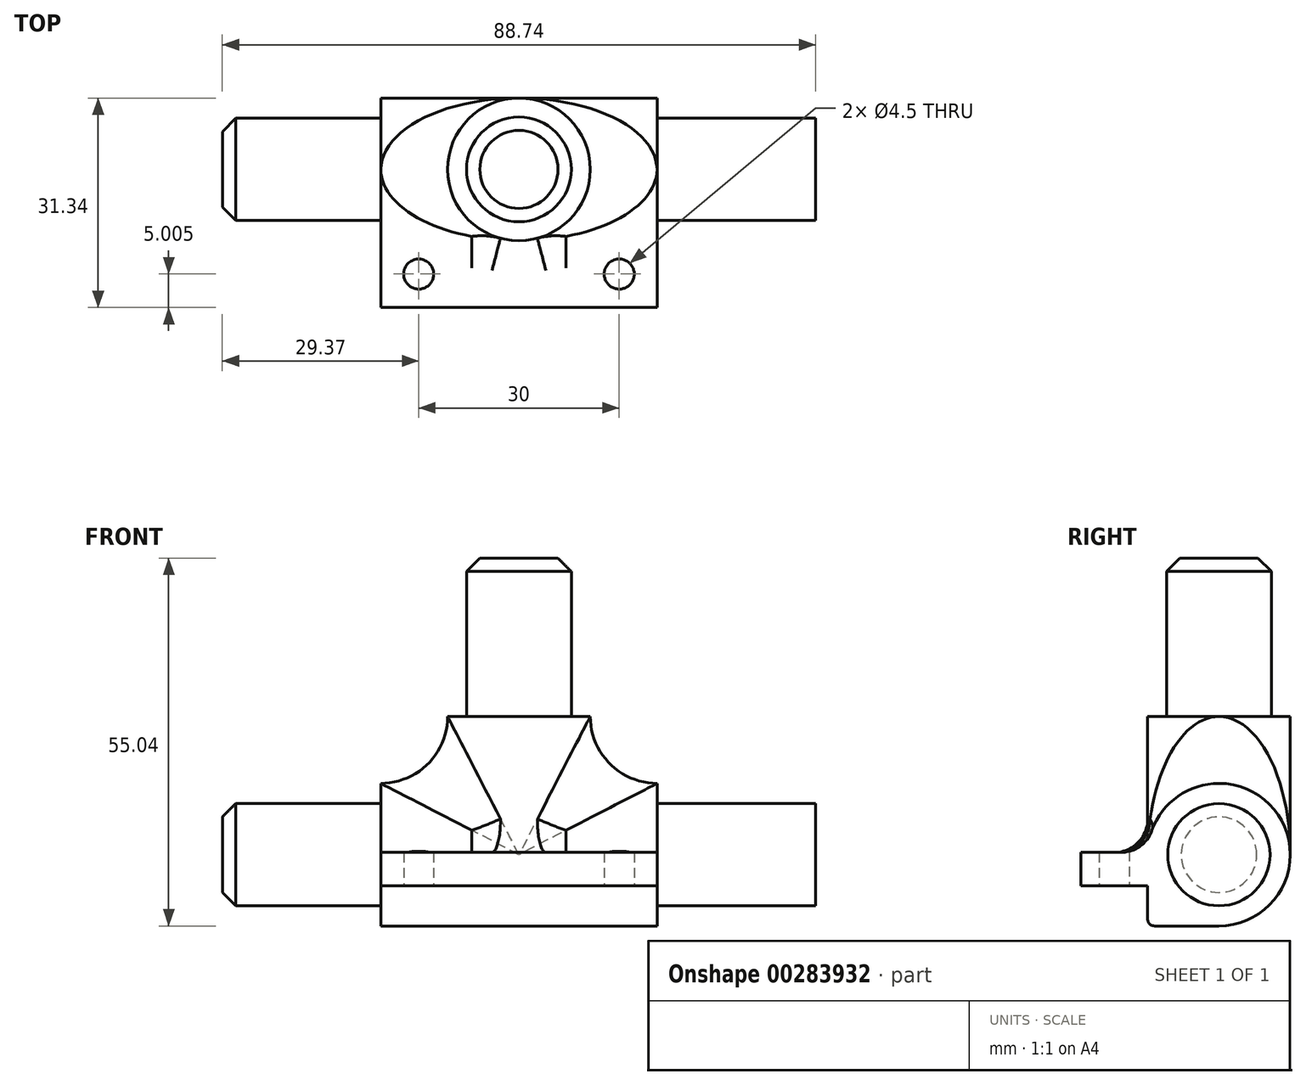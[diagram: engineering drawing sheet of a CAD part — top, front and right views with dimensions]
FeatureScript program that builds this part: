
annotation { "Feature Type Name" : "Feature", "Feature Type Description" : "" }
export const myFeature = defineFeature(function(context is Context, id is Id, definition is map)
    precondition{}
    {
        {
            var Q0;
            Q0=qCreatedBy(makeId("Right.planeOp"),FACE);
            var sketch = newSketch(context, id + "F0", { "sketchPlane" : qUnion([Q0])});
            skCircle(sketch, "E0", {"center": v(0, 0) * mm, "radius": 10.67 * mm});
            skSolve(sketch);
        }
        {
            var Q0;
            Q0 = qSketchRegion(id + "F0", true);
            extrude(context, id + "F1", {"entities" : qUnion([Q0]), "endBound" : BoundingType.SYMMETRIC, "depth" : 21.34 * mm + 20 * mm});
        }
        {
            var Q0;
            Q0=makeQuery(id+"F1.opExtrude","CAP_FACE",FACE,{"disambiguationData":[OSD([sQuery(id+"F0.wireOp",EDGE,"E0")])],"isStart":false});
            var sketch = newSketch(context, id + "F2", { "sketchPlane" : qUnion([Q0])});
            skCircle(sketch, "E1", {"center": v(0, 0) * mm, "radius": 7.9 * mm});
            skSolve(sketch);
        }
        {
            var Q0;
            Q0 = qSketchRegion(id + "F2", true);
            extrude(context, id + "F3", {"entities" : qUnion([Q0]), "operationType" : NewBodyOperationType.ADD, "depth" : 15.8 * mm * 1.5});
        }
        {
            var Q0;
            Q0=makeQuery(id+"F3.opExtrude","CAP_FACE",FACE,{"disambiguationData":[OSD([sQuery(id+"F2.wireOp",EDGE,"E1")])],"isStart":false});
            var sketch = newSketch(context, id + "F4", { "sketchPlane" : qUnion([Q0])});
            skCircle(sketch, "E2.0", {"center": v(0, 0) * mm, "radius": 7.9 * mm});
            skCircle(sketch, "E3", {"center": v(0, 0) * mm, "radius": 7.65 * mm});
            skSolve(sketch);
        }
        {
            var Q0;
            Q0 = qSketchRegion(id + "F4", true);
            var Q1;
            Q1=makeQuery(id+"F1.opExtrude","CAP_FACE",FACE,{"disambiguationData":[OSD([sQuery(id+"F0.wireOp",EDGE,"E0")])],"isStart":false});
            extrude(context, id + "F5", {"entities" : qUnion([Q0]), "operationType" : NewBodyOperationType.REMOVE, "endBound" : BoundingType.UP_TO_SURFACE, "oppositeDirection" : true, "endBoundEntityFace" : qUnion([Q1]), "depth" : 25 * mm});
        }
        {
            var Q0;
            Q0=makeQuery(id+"F1.opExtrude","CAP_FACE",FACE,{"disambiguationData":[OSD([sQuery(id+"F0.wireOp",EDGE,"E0")])],"isStart":true});
            var sketch = newSketch(context, id + "F6", { "sketchPlane" : qUnion([Q0])});
            skCircle(sketch, "E4", {"center": v(0, 0) * mm, "radius": 7.65 * mm});
            skSolve(sketch);
        }
        {
            var Q0;
            Q0 = qSketchRegion(id + "F6", true);
            extrude(context, id + "F7", {"entities" : qUnion([Q0]), "operationType" : NewBodyOperationType.ADD, "depth" : 15.8 * mm * 1.5});
        }
        {
            var Q0;
            Q0=qCreatedBy(makeId("Top.planeOp"),FACE);
            var sketch = newSketch(context, id + "F8", { "sketchPlane" : qUnion([Q0])});
            skCircle(sketch, "E5", {"center": v(0, 0) * mm, "radius": 10.67 * mm});
            skSolve(sketch);
        }
        {
            var Q0;
            Q0 = qSketchRegion(id + "F8", true);
            extrude(context, id + "F9", {"entities" : qUnion([Q0]), "operationType" : NewBodyOperationType.ADD, "depth" : 21.34 * mm / 2 + 10 * mm});
        }
        {
            var Q0;
            Q0=makeQuery(id+"F9.opExtrude","CAP_FACE",FACE,{"disambiguationData":[OSD([sQuery(id+"F8.wireOp",EDGE,"E5")])],"isStart":false});
            var sketch = newSketch(context, id + "F10", { "sketchPlane" : qUnion([Q0])});
            skCircle(sketch, "E6", {"center": v(0, 0) * mm, "radius": 7.84 * mm});
            skSolve(sketch);
        }
        {
            var Q0;
            Q0 = qSketchRegion(id + "F10", true);
            extrude(context, id + "F11", {"entities" : qUnion([Q0]), "operationType" : NewBodyOperationType.ADD, "depth" : 15.8 * mm * 1.5});
        }
        {
            var Q0;
            Q0=makeQuery(id+"F11.opExtrude","CAP_EDGE",EDGE,{"disambiguationData":[OSD([sQuery(id+"F10.wireOp",EDGE,"E6")])],"isStart":false});
            var Q1;
            Q1=makeQuery(id+"F5.boolean.opBoolean","COPY",EDGE,{"derivedFrom":makeQuery(id+"F5.opExtrude","CAP_EDGE",EDGE,{"disambiguationData":[OSD([sQuery(id+"F4.wireOp",EDGE,"E3")])],"isStart":true})});
            var Q2;
            Q2=makeQuery(id+"F7.opExtrude","CAP_EDGE",EDGE,{"disambiguationData":[OSD([sQuery(id+"F6.wireOp",EDGE,"E4")])],"isStart":false});
            chamfer(context, id + "F12", {"entities" : qUnion([Q0, Q1, Q2]), "width" : 2 * mm, "tangentPropagation" : true});
        }
        {
            var Q0;
            Q0=makeQuery(id+"F9.boolean.opBoolean","INTERSECT",EDGE,{"disambiguationData":[OD(0.0)],"derivedFrom":[makeQuery(id+"F1.opExtrude","SWEPT_FACE",FACE,{"disambiguationData":[OSD([sQuery(id+"F0.wireOp",EDGE,"E0")])]}),makeQuery(id+"F9.opExtrude","SWEPT_FACE",FACE,{"disambiguationData":[OSD([sQuery(id+"F8.wireOp",EDGE,"E5")])]})]});
            var Q1;
            Q1=makeQuery(id+"F9.boolean.opBoolean","INTERSECT",EDGE,{"disambiguationData":[OD(1.0)],"derivedFrom":[makeQuery(id+"F1.opExtrude","SWEPT_FACE",FACE,{"disambiguationData":[OSD([sQuery(id+"F0.wireOp",EDGE,"E0")])]}),makeQuery(id+"F9.opExtrude","SWEPT_FACE",FACE,{"disambiguationData":[OSD([sQuery(id+"F8.wireOp",EDGE,"E5")])]})]});
            fillet(context, id + "F13", {"entities" : qUnion([Q0, Q1]), "radius" : 10 * mm, "tangentPropagation" : true, "allowEdgeOverflow" : false});
        }
        {
            var Q0;
            Q0=qCreatedBy(makeId("Right.planeOp"),FACE);
            var sketch = newSketch(context, id + "F14", { "sketchPlane" : qUnion([Q0])});
            skCircle(sketch, "E7.0", {"center": v(0, 0) * mm, "radius": 10.67 * mm, "construction": true});
            skLineSegment(sketch, "E8", {"start": v(0, 0) * mm, "end": v(0, -10.67) * mm, "construction": true});
            skLineSegment(sketch, "E9", {"start": v(0, -10.67) * mm, "end": v(-33.08, -10.67) * mm, "construction": true});
            skLineSegment(sketch, "E10.bottom", {"start": v(0, -4.67) * mm, "end": v(-20.67, -4.67) * mm});
            skLineSegment(sketch, "E10.top", {"start": v(0, 0.33) * mm, "end": v(-20.67, 0.33) * mm});
            skLineSegment(sketch, "E10.left", {"start": v(0, -4.67) * mm, "end": v(0, 0.33) * mm});
            skLineSegment(sketch, "E10.right", {"start": v(-20.67, -4.67) * mm, "end": v(-20.67, 0.33) * mm});
            skPoint(sketch, "E11", {"position": v(-10.67, 0) * mm});
            skSolve(sketch);
        }
        {
            var Q0;
            Q0 = qSketchRegion(id + "F14", true);
            var Q1;
            {var subQ0=sQuery(id+"F0.wireOp",EDGE,"E0");Q1=makeQuery(id+"F5.boolean.opBoolean","MERGE",FACE,{"derivedFrom":[makeQuery(id+"F1.opExtrude","CAP_FACE",FACE,{"disambiguationData":[OSD([subQ0])],"isStart":false}),makeQuery(id+"F5.opExtrude","CAP_FACE",FACE,{"disambiguationData":[OSD([subQ0])],"isStart":false})]});}
            var Q2;
            Q2=makeQuery(id+"F1.opExtrude","CAP_FACE",FACE,{"disambiguationData":[OSD([sQuery(id+"F0.wireOp",EDGE,"E0")])],"isStart":true});
            extrude(context, id + "F15", {"entities" : qUnion([Q0]), "operationType" : NewBodyOperationType.ADD, "endBound" : BoundingType.UP_TO_SURFACE, "endBoundEntityFace" : qUnion([Q1]), "depth" : 20 * mm + 21.59 * mm, "hasSecondDirection" : true, "secondDirectionBound" : SecondDirectionBoundingType.UP_TO_SURFACE, "secondDirectionOppositeDirection" : true, "secondDirectionBoundEntityFace" : qUnion([Q2]), "secondDirectionDepth" : 25 * mm});
        }
        {
            var Q0;
            {var subQ0=sQuery(id+"F0.wireOp",EDGE,"E0");Q0=makeQuery(id+"F15.boolean.opBoolean","MERGE",FACE,{"derivedFrom":[makeQuery(id+"F1.opExtrude","CAP_FACE",FACE,{"disambiguationData":[OSD([subQ0])],"isStart":true}),makeQuery(id+"F15.opExtrude","CAP_FACE",FACE,{"disambiguationData":[OSD([subQ0])],"isStart":true})]});}
            var sketch = newSketch(context, id + "F16", { "sketchPlane" : qUnion([Q0])});
            skLineSegment(sketch, "E12", {"start": v(0, -10.67) * mm, "end": v(10.66, -10.67) * mm});
            skArc(sketch, "E13.0", {"start": v(10.66, -0.33) * mm, "mid": v(7.43, -7.66) * mm, "end": v(0, -10.67) * mm});
            skPoint(sketch, "E14.orphan", {"position": v(0, 10.67) * mm});
            skCircle(sketch, "E15", {"center": v(0, 0) * mm, "radius": 10.67 * mm, "construction": true});
            skLineSegment(sketch, "E16", {"start": v(0, 0) * mm, "end": v(10.66, -0.33) * mm, "construction": true});
            skLineSegment(sketch, "E17", {"start": v(10.66, -0.33) * mm, "end": v(10.66, -10.67) * mm});
            skSolve(sketch);
        }
        {
            var Q0;
            Q0 = qSketchRegion(id + "F16", true);
            var Q1;
            {var subQ0=sQuery(id+"F0.wireOp",EDGE,"E0");Q1=makeQuery(id+"F15.boolean.opBoolean","MERGE",FACE,{"derivedFrom":[makeQuery(id+"F5.boolean.opBoolean","MERGE",FACE,{"derivedFrom":[makeQuery(id+"F1.opExtrude","CAP_FACE",FACE,{"disambiguationData":[OSD([subQ0])],"isStart":false}),makeQuery(id+"F5.opExtrude","CAP_FACE",FACE,{"disambiguationData":[OSD([subQ0])],"isStart":false})]}),makeQuery(id+"F15.opExtrude","CAP_FACE",FACE,{"disambiguationData":[OSD([subQ0])],"isStart":false})]});}
            extrude(context, id + "F17", {"entities" : qUnion([Q0]), "operationType" : NewBodyOperationType.ADD, "endBound" : BoundingType.UP_TO_SURFACE, "oppositeDirection" : true, "endBoundEntityFace" : qUnion([Q1]), "depth" : 25 * mm});
        }
        {
            var Q0;
            {var subQ0=sQuery(id+"F0.wireOp",EDGE,"E0");Q0=makeQuery(id+"F15.opExtrude","TWEAK_EDGE",EDGE,{"derivedFrom":[makeQuery(id+"F5.boolean.opBoolean","MERGE",FACE,{"derivedFrom":[makeQuery(id+"F1.opExtrude","CAP_FACE",FACE,{"disambiguationData":[OSD([subQ0])],"isStart":false}),makeQuery(id+"F5.opExtrude","CAP_FACE",FACE,{"disambiguationData":[OSD([subQ0])],"isStart":false})]}),makeQuery(id+"F14.imprint","IMPRINT",EDGE,{"derivedFrom":sQuery(id+"F14.wireOp",EDGE,"E10.right")})]});}
            var Q1;
            Q1=makeQuery(id+"F15.opExtrude","TWEAK_EDGE",EDGE,{"derivedFrom":[makeQuery(id+"F1.opExtrude","CAP_FACE",FACE,{"disambiguationData":[OSD([sQuery(id+"F0.wireOp",EDGE,"E0")])],"isStart":true}),makeQuery(id+"F14.imprint","IMPRINT",EDGE,{"derivedFrom":sQuery(id+"F14.wireOp",EDGE,"E10.right")})]});
            var Q2;
            Q2=makeQuery(id+"F15.boolean.opBoolean","INTERSECT",EDGE,{"disambiguationData":[OD(0.0)],"derivedFrom":[makeQuery(id+"F1.opExtrude","SWEPT_FACE",FACE,{"disambiguationData":[OSD([sQuery(id+"F0.wireOp",EDGE,"E0")])]}),makeQuery(id+"F15.opExtrude","SWEPT_FACE",FACE,{"disambiguationData":[OSD([sQuery(id+"F14.wireOp",EDGE,"E10.top")])]})]});
            fillet(context, id + "F18", {"entities" : qUnion([Q0, Q1, Q2]), "radius" : 5 * mm, "tangentPropagation" : true, "allowEdgeOverflow" : false});
        }
        {
            var Q0;
            Q0=makeQuery(id+"F17.opExtrude","SWEPT_EDGE",EDGE,{"disambiguationData":[OSD([sQuery(id+"F16.wireOp",EDGE,"E12"),sQuery(id+"F16.wireOp",EDGE,"N2ObjeJH-o0BS-Ub8t-eQPJ-StFMS2llRFrs")])]});
            fillet(context, id + "F19", {"entities" : qUnion([Q0]), "radius" : 1 * mm, "tangentPropagation" : true, "allowEdgeOverflow" : false});
        }
        {
            var Q0;
            Q0=makeQuery(id+"F15.opExtrude","SWEPT_FACE",FACE,{"disambiguationData":[OSD([sQuery(id+"F14.wireOp",EDGE,"E10.bottom")])]});
            var sketch = newSketch(context, id + "F20", { "sketchPlane" : qUnion([Q0])});
            skLineSegment(sketch, "E18", {"start": v(0, 20.67) * mm, "end": v(0, 10.66) * mm, "construction": true});
            skLineSegment(sketch, "E19", {"start": v(0, 15.67) * mm, "end": v(20.67, 15.67) * mm, "construction": true});
            skCircle(sketch, "E20", {"center": v(-15, 15.67) * mm, "radius": 2.25 * mm});
            skCircle(sketch, "E21.MirrorC", {"center": v(15, 15.67) * mm, "radius": 2.25 * mm});
            skSolve(sketch);
        }
        {
            var Q0;
            Q0 = qSketchRegion(id + "F20", true);
            extrude(context, id + "F21", {"entities" : qUnion([Q0]), "operationType" : NewBodyOperationType.REMOVE, "endBound" : BoundingType.THROUGH_ALL, "oppositeDirection" : true, "depth" : 25 * mm});
        }
    });
